# Revit family: 251507.03 Alarmsender Safetel airborne DC8M
name_source: partatom
category: Fire Alarm Devices
revit_build: Autodesk Revit 2016 (Build: 20160314_0715(x64)
units: mm (PartAtom-declared; Revit-internal decimal feet)

## family parameters
Always vertical = No
Cut with Voids When Loaded = No
Maintain Annotation Orientation = Yes
OmniClass Number = 23.85.30.21.11.17
OmniClass Title = Other Components
Part Type = Normal
Room Calculation Point = No
Round Connector Dimension = Use Diameter
Shared = No
Work Plane-Based = No

## types (1)
- Alarmsender
    Assembly Code = 5423
    Keynote = XN4
    Manufacturer = Honeywell
    NS8360 = 5423_XN4
    NV Length A = 158 mm  [stored 0.518373 ft]
    NV Length B = 162 mm  [stored 0.531496 ft]
    NV Length C = 58 mm  [stored 0.190289 ft]
    NV Material = White
    NV Type = AS
    NV Type tekst synlig = Yes
    Type Comments = -OM

note: [stored X ft] marks values corroborated as IEEE doubles in the binary element streams (Revit-internal decimal feet)

## geometry (parser evidence)
native form markers: Blend x4, Sweep x6
no freeform markers — native parametric forms only
